# Revit family: 122
name_source: partatom
category: Casework
units: mm (PartAtom-declared; Revit-internal decimal feet)

## family parameters
Always vertical = Yes
Cut with Voids When Loaded = No
Room Calculation Point = No
Shared = No
Work Plane-Based = No

## types (1)
- 122
    Assembly Code = E2010200
    Back Panel Material = <By Category>
    Cab Door - Height = 2' - 6 1/2"
    Cab Door - Style = Cabinet Door_ Flush : Horizontal Center Handle
    Cab Door - Thickness = 0' - 0"
    Cab Door - Width = 1' - 5 7/8"
    Cab Hardware Finish = <By Category>
    Counter Thickness = 0' - 1 1/2"
    Default Elevation = 0' - 0"
    Depth = 2' - 0"
    Description = Base Cabinet w/o Drawers
    Door Panel Material = <By Category>
    Height = 2' - 10 1/2"
    Manufacturer = Woodwork Institute
    Model = 122
    NAAWS Depth = 24
    NAAWS Height = 36
    NAAWS Width = 36
    Shelf Panel Material = <By Category>
    Side Panel Material = <By Category>
    Toe Panel Material = <By Category>
    Top Panel Material = <By Category>
    URL = www.wicnet.org/manual_sections.asp
    Width = 3' - 0"

## geometry (parser evidence)
native form markers: Sweep x22
no freeform markers — native parametric forms only
